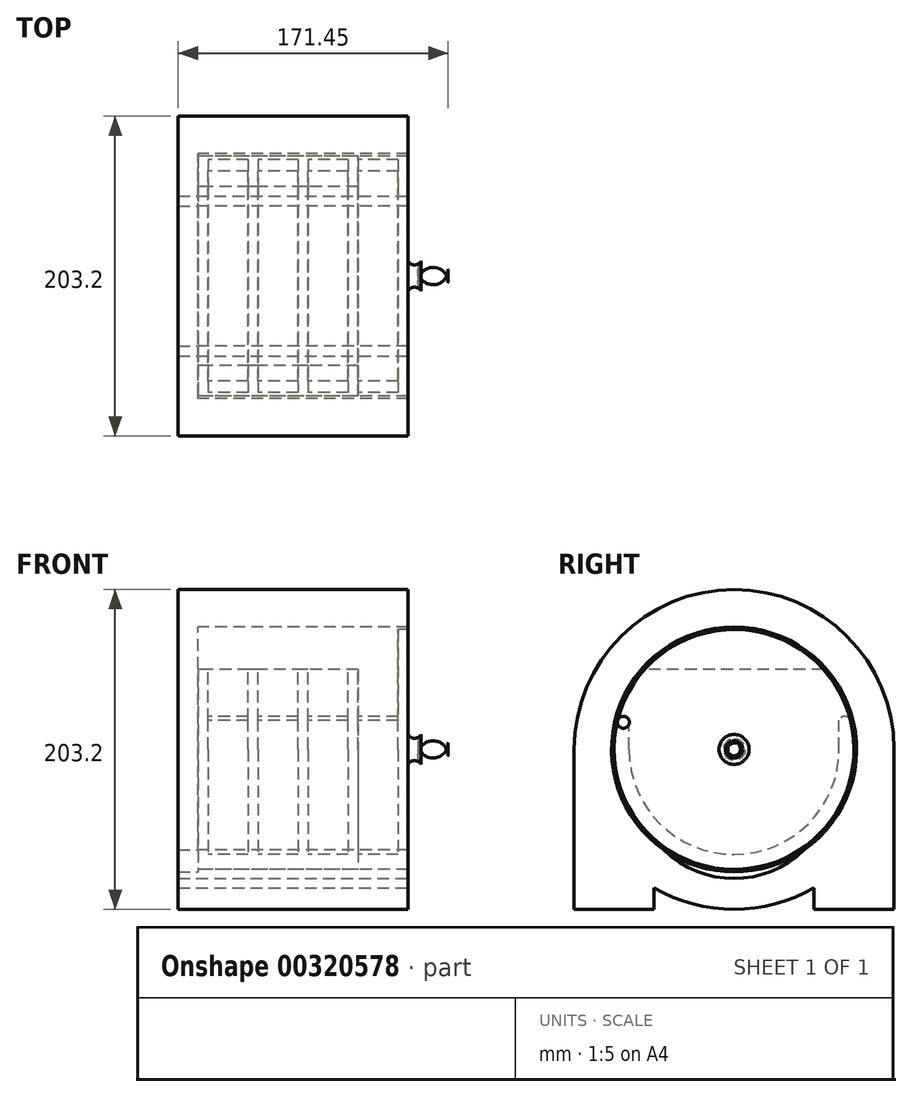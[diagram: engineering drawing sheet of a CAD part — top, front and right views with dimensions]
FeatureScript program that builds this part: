
annotation { "Feature Type Name" : "Feature", "Feature Type Description" : "" }
export const myFeature = defineFeature(function(context is Context, id is Id, definition is map)
    precondition{}
    {
        {
            var Q0;
            Q0=qCreatedBy(makeId("Right.planeOp"),FACE);
            var sketch = newSketch(context, id + "F0", { "sketchPlane" : qUnion([Q0])});
            skCircle(sketch, "E0", {"center": v(0, 0) * mm, "radius": 76.2 * mm});
            skLineSegment(sketch, "E1", {"start": v(0, 76.2) * mm, "end": v(0, 50.8) * mm});
            skLineSegment(sketch, "E2", {"start": v(56.8, 50.8) * mm, "end": v(-56.8, 50.8) * mm});
            skSolve(sketch);
        }
        {
            var Q0;
            {var subQ0=sQuery(id+"F0.wireOp",EDGE,"E2");var subQ1=sQuery(id+"F0.wireOp",EDGE,"E0");var subQ2=makeQuery(id+"F0.imprint","INTERSECT",VERTEX,{"disambiguationData":[OD(0.0)],"derivedFrom":[subQ1,subQ0]});Q0=makeQuery(id+"F0.imprint","IMPRINT",FACE,{"disambiguationData":[TD([[makeQuery(id+"F0.imprint","IMPRINT",EDGE,{"disambiguationData":[TD([[subQ2,1.0]])],"derivedFrom":subQ1}),1.0]])]});}
            extrude(context, id + "F1", {"entities" : qUnion([Q0]), "depth" : 6.35 * mm});
        }
        {
            var Q0;
            Q0=makeQuery(id+"F1.opExtrude","CAP_FACE",FACE,{"disambiguationData":[OSD([sQuery(id+"F0.wireOp",EDGE,"E0"),sQuery(id+"F0.wireOp",EDGE,"E2")])],"isStart":false});
            var sketch = newSketch(context, id + "F2", { "sketchPlane" : qUnion([Q0])});
            skCircle(sketch, "E3", {"center": v(0, 0) * mm, "radius": 76.2 * mm});
            skCircle(sketch, "E4.0", {"center": v(0, 0) * mm, "radius": 66.67 * mm});
            skLineSegment(sketch, "E5", {"start": v(-66.67, 0) * mm, "end": v(-66.67, 36.9) * mm});
            skLineSegment(sketch, "E6", {"start": v(66.67, 0) * mm, "end": v(66.67, 36.9) * mm});
            skArc(sketch, "E7", {"start": v(73.93, 18.45) * mm, "mid": v(70.3, 21.1) * mm, "end": v(66.67, 18.45) * mm});
            skPoint(sketch, "E7.startSnap0", {"position": v(66.67, 18.45) * mm});
            skArc(sketch, "E8", {"start": v(-66.67, 18.45) * mm, "mid": v(-70.3, 21.1) * mm, "end": v(-73.93, 18.45) * mm});
            skPoint(sketch, "E8.endSnap0", {"position": v(-66.67, 18.45) * mm});
            skSolve(sketch);
        }
        {
            var Q0;
            {var subQ3=sQuery(id+"F2.wireOp",EDGE,"E7");Q0=makeQuery(id+"F2.imprint","IMPRINT",FACE,{"disambiguationData":[TD([[makeQuery(id+"F2.imprint","IMPRINT",EDGE,{"derivedFrom":subQ3}),1.0]])]});}
            extrude(context, id + "F3", {"entities" : qUnion([Q0]), "operationType" : NewBodyOperationType.ADD, "depth" : 25.4 * mm});
        }
        {
            var Q0;
            Q0=makeQuery(id+"F3.opExtrude","CAP_FACE",FACE,{"disambiguationData":[OSD([sQuery(id+"F2.wireOp",EDGE,"E3"),sQuery(id+"F2.wireOp",EDGE,"E4.0"),sQuery(id+"F2.wireOp",EDGE,"E5"),sQuery(id+"F2.wireOp",EDGE,"E6"),sQuery(id+"F2.wireOp",EDGE,"E7"),sQuery(id+"F2.wireOp",EDGE,"E8")])],"isStart":false});
            var sketch = newSketch(context, id + "F4", { "sketchPlane" : qUnion([Q0])});
            skCircle(sketch, "E9", {"center": v(0, 0) * mm, "radius": 76.2 * mm});
            skLineSegment(sketch, "E10", {"start": v(0, 76.2) * mm, "end": v(0, 50.8) * mm});
            skLineSegment(sketch, "E11", {"start": v(56.8, 50.8) * mm, "end": v(-56.8, 50.8) * mm});
            skSolve(sketch);
        }
        {
            var Q0;
            Q0=makeQuery(id+"F4.imprint","IMPRINT",FACE,{"disambiguationData":[TD([[makeQuery(id+"F4.imprint","IMPRINT",EDGE,{"derivedFrom":makeQuery(id+"F3.opExtrude","CAP_EDGE",EDGE,{"disambiguationData":[OSD([sQuery(id+"F2.wireOp",EDGE,"E4.0")])],"isStart":false})}),-1.0]])]});
            var Q1;
            Q1=makeQuery(id+"F4.imprint","IMPRINT",FACE,{"disambiguationData":[TD([[makeQuery(id+"F4.imprint","IMPRINT",EDGE,{"derivedFrom":makeQuery(id+"F3.opExtrude","CAP_EDGE",EDGE,{"disambiguationData":[OSD([sQuery(id+"F2.wireOp",EDGE,"E4.0")])],"isStart":false})}),1.0]])]});
            extrude(context, id + "F5", {"entities" : qUnion([Q0, Q1]), "operationType" : NewBodyOperationType.ADD, "depth" : 6.35 * mm});
        }
        {
            var Q0;
            Q0=makeQuery(id+"F5.opExtrude","CAP_FACE",FACE,{"disambiguationData":[OSD([sQuery(id+"F4.wireOp",EDGE,"E9"),sQuery(id+"F4.wireOp",EDGE,"E11")])],"isStart":false});
            var sketch = newSketch(context, id + "F6", { "sketchPlane" : qUnion([Q0])});
            skCircle(sketch, "E12", {"center": v(0, 0) * mm, "radius": 76.2 * mm});
            skCircle(sketch, "E13.0", {"center": v(0, 0) * mm, "radius": 66.67 * mm});
            skLineSegment(sketch, "E14", {"start": v(-66.67, 0) * mm, "end": v(-66.67, 36.9) * mm});
            skLineSegment(sketch, "E15", {"start": v(66.67, 0) * mm, "end": v(66.67, 36.9) * mm});
            skArc(sketch, "E16", {"start": v(73.93, 18.45) * mm, "mid": v(70.3, 21.1) * mm, "end": v(66.67, 18.45) * mm});
            skPoint(sketch, "E16.startSnap0", {"position": v(66.67, 18.45) * mm});
            skArc(sketch, "E17", {"start": v(-66.67, 18.45) * mm, "mid": v(-70.3, 21.1) * mm, "end": v(-73.93, 18.45) * mm});
            skPoint(sketch, "E17.endSnap0", {"position": v(-66.67, 18.45) * mm});
            skSolve(sketch);
        }
        {
            var Q0;
            {var subQ3=sQuery(id+"F6.wireOp",EDGE,"E16");Q0=makeQuery(id+"F6.imprint","IMPRINT",FACE,{"disambiguationData":[TD([[makeQuery(id+"F6.imprint","IMPRINT",EDGE,{"derivedFrom":subQ3}),1.0]])]});}
            extrude(context, id + "F7", {"entities" : qUnion([Q0]), "operationType" : NewBodyOperationType.ADD, "depth" : 25.4 * mm});
        }
        {
            var Q0;
            Q0=makeQuery(id+"F7.opExtrude","CAP_FACE",FACE,{"disambiguationData":[OSD([sQuery(id+"F6.wireOp",EDGE,"E12"),sQuery(id+"F6.wireOp",EDGE,"E13.0"),sQuery(id+"F6.wireOp",EDGE,"E14"),sQuery(id+"F6.wireOp",EDGE,"E15"),sQuery(id+"F6.wireOp",EDGE,"E16"),sQuery(id+"F6.wireOp",EDGE,"E17")])],"isStart":false});
            var sketch = newSketch(context, id + "F8", { "sketchPlane" : qUnion([Q0])});
            skCircle(sketch, "E18", {"center": v(0, 0) * mm, "radius": 76.2 * mm});
            skLineSegment(sketch, "E19", {"start": v(0, 76.2) * mm, "end": v(0, 50.8) * mm});
            skLineSegment(sketch, "E20", {"start": v(56.8, 50.8) * mm, "end": v(-56.8, 50.8) * mm});
            skSolve(sketch);
        }
        {
            var Q0;
            Q0=makeQuery(id+"F8.imprint","IMPRINT",FACE,{"disambiguationData":[TD([[makeQuery(id+"F8.imprint","IMPRINT",EDGE,{"derivedFrom":makeQuery(id+"F7.opExtrude","CAP_EDGE",EDGE,{"disambiguationData":[OSD([sQuery(id+"F6.wireOp",EDGE,"E13.0")])],"isStart":false})}),-1.0]])]});
            var Q1;
            Q1=makeQuery(id+"F8.imprint","IMPRINT",FACE,{"disambiguationData":[TD([[makeQuery(id+"F8.imprint","IMPRINT",EDGE,{"derivedFrom":makeQuery(id+"F7.opExtrude","CAP_EDGE",EDGE,{"disambiguationData":[OSD([sQuery(id+"F6.wireOp",EDGE,"E13.0")])],"isStart":false})}),1.0]])]});
            extrude(context, id + "F9", {"entities" : qUnion([Q0, Q1]), "operationType" : NewBodyOperationType.ADD, "depth" : 6.35 * mm});
        }
        {
            var Q0;
            Q0=makeQuery(id+"F9.opExtrude","CAP_FACE",FACE,{"disambiguationData":[OSD([sQuery(id+"F8.wireOp",EDGE,"E18"),sQuery(id+"F8.wireOp",EDGE,"E20")])],"isStart":false});
            var sketch = newSketch(context, id + "F10", { "sketchPlane" : qUnion([Q0])});
            skCircle(sketch, "E21", {"center": v(0, 0) * mm, "radius": 76.2 * mm});
            skCircle(sketch, "E22.0", {"center": v(0, 0) * mm, "radius": 66.67 * mm});
            skLineSegment(sketch, "E23", {"start": v(-66.68, 0) * mm, "end": v(-66.68, 36.9) * mm});
            skLineSegment(sketch, "E24", {"start": v(66.67, 0) * mm, "end": v(66.67, 36.9) * mm});
            skArc(sketch, "E25", {"start": v(73.93, 18.45) * mm, "mid": v(70.3, 21.1) * mm, "end": v(66.68, 18.45) * mm});
            skPoint(sketch, "E25.startSnap0", {"position": v(66.67, 18.45) * mm});
            skArc(sketch, "E26", {"start": v(-66.68, 18.45) * mm, "mid": v(-70.3, 21.1) * mm, "end": v(-73.93, 18.45) * mm});
            skPoint(sketch, "E26.endSnap0", {"position": v(-66.68, 18.45) * mm});
            skSolve(sketch);
        }
        {
            var Q0;
            {var subQ3=sQuery(id+"F10.wireOp",EDGE,"E25");Q0=makeQuery(id+"F10.imprint","IMPRINT",FACE,{"disambiguationData":[TD([[makeQuery(id+"F10.imprint","IMPRINT",EDGE,{"derivedFrom":subQ3}),1.0]])]});}
            extrude(context, id + "F11", {"entities" : qUnion([Q0]), "operationType" : NewBodyOperationType.ADD, "depth" : 25.4 * mm});
        }
        {
            var Q0;
            Q0=makeQuery(id+"F11.opExtrude","CAP_FACE",FACE,{"disambiguationData":[OSD([sQuery(id+"F10.wireOp",EDGE,"E21"),sQuery(id+"F10.wireOp",EDGE,"E22.0"),sQuery(id+"F10.wireOp",EDGE,"E23"),sQuery(id+"F10.wireOp",EDGE,"E24"),sQuery(id+"F10.wireOp",EDGE,"E25"),sQuery(id+"F10.wireOp",EDGE,"E26")])],"isStart":false});
            var sketch = newSketch(context, id + "F12", { "sketchPlane" : qUnion([Q0])});
            skCircle(sketch, "E27", {"center": v(0, 0) * mm, "radius": 76.2 * mm});
            skLineSegment(sketch, "E28", {"start": v(0, 76.2) * mm, "end": v(0, 50.8) * mm});
            skLineSegment(sketch, "E29", {"start": v(56.8, 50.8) * mm, "end": v(-56.8, 50.8) * mm});
            skSolve(sketch);
        }
        {
            var Q0;
            Q0=makeQuery(id+"F12.imprint","IMPRINT",FACE,{"disambiguationData":[TD([[makeQuery(id+"F12.imprint","IMPRINT",EDGE,{"derivedFrom":makeQuery(id+"F11.opExtrude","CAP_EDGE",EDGE,{"disambiguationData":[OSD([sQuery(id+"F10.wireOp",EDGE,"E22.0")])],"isStart":false})}),-1.0]])]});
            var Q1;
            Q1=makeQuery(id+"F12.imprint","IMPRINT",FACE,{"disambiguationData":[TD([[makeQuery(id+"F12.imprint","IMPRINT",EDGE,{"derivedFrom":makeQuery(id+"F11.opExtrude","CAP_EDGE",EDGE,{"disambiguationData":[OSD([sQuery(id+"F10.wireOp",EDGE,"E22.0")])],"isStart":false})}),1.0]])]});
            extrude(context, id + "F13", {"entities" : qUnion([Q0, Q1]), "operationType" : NewBodyOperationType.ADD, "depth" : 6.35 * mm});
        }
        {
            var Q0;
            Q0=makeQuery(id+"F13.opExtrude","CAP_FACE",FACE,{"disambiguationData":[OSD([sQuery(id+"F12.wireOp",EDGE,"E27"),sQuery(id+"F12.wireOp",EDGE,"E29")])],"isStart":false});
            var sketch = newSketch(context, id + "F14", { "sketchPlane" : qUnion([Q0])});
            skCircle(sketch, "E30", {"center": v(0, 0) * mm, "radius": 76.2 * mm});
            skCircle(sketch, "E31.0", {"center": v(0, 0) * mm, "radius": 66.67 * mm});
            skLineSegment(sketch, "E32", {"start": v(-66.67, 0) * mm, "end": v(-66.67, 36.9) * mm});
            skLineSegment(sketch, "E33", {"start": v(66.67, 0) * mm, "end": v(66.67, 36.9) * mm});
            skArc(sketch, "E34", {"start": v(73.93, 18.45) * mm, "mid": v(70.3, 21.1) * mm, "end": v(66.68, 18.45) * mm});
            skPoint(sketch, "E34.startSnap0", {"position": v(66.67, 18.45) * mm});
            skArc(sketch, "E35", {"start": v(-66.67, 18.45) * mm, "mid": v(-70.3, 21.1) * mm, "end": v(-73.93, 18.45) * mm});
            skPoint(sketch, "E35.endSnap0", {"position": v(-66.68, 18.45) * mm});
            skSolve(sketch);
        }
        {
            var Q0;
            {var subQ3=sQuery(id+"F14.wireOp",EDGE,"E34");Q0=makeQuery(id+"F14.imprint","IMPRINT",FACE,{"disambiguationData":[TD([[makeQuery(id+"F14.imprint","IMPRINT",EDGE,{"derivedFrom":subQ3}),1.0]])]});}
            extrude(context, id + "F15", {"entities" : qUnion([Q0]), "operationType" : NewBodyOperationType.ADD, "depth" : 25.4 * mm});
        }
        {
            var Q0;
            Q0=makeQuery(id+"F15.opExtrude","CAP_FACE",FACE,{"disambiguationData":[OSD([sQuery(id+"F14.wireOp",EDGE,"E30"),sQuery(id+"F14.wireOp",EDGE,"E31.0"),sQuery(id+"F14.wireOp",EDGE,"E32"),sQuery(id+"F14.wireOp",EDGE,"E33"),sQuery(id+"F14.wireOp",EDGE,"E34"),sQuery(id+"F14.wireOp",EDGE,"E35")])],"isStart":false});
            var sketch = newSketch(context, id + "F16", { "sketchPlane" : qUnion([Q0])});
            skCircle(sketch, "E36", {"center": v(0, 0) * mm, "radius": 76.2 * mm});
            skLineSegment(sketch, "E37", {"start": v(0, 76.2) * mm, "end": v(0, 50.8) * mm});
            skLineSegment(sketch, "E38", {"start": v(56.8, 50.8) * mm, "end": v(-56.8, 50.8) * mm});
            skSolve(sketch);
        }
        {
            var Q0;
            Q0=makeQuery(id+"F16.imprint","IMPRINT",FACE,{"disambiguationData":[TD([[makeQuery(id+"F16.imprint","IMPRINT",EDGE,{"derivedFrom":makeQuery(id+"F15.opExtrude","CAP_EDGE",EDGE,{"disambiguationData":[OSD([sQuery(id+"F14.wireOp",EDGE,"E31.0")])],"isStart":false})}),-1.0]])]});
            var Q1;
            Q1=makeQuery(id+"F16.imprint","IMPRINT",FACE,{"disambiguationData":[TD([[makeQuery(id+"F16.imprint","IMPRINT",EDGE,{"derivedFrom":makeQuery(id+"F15.opExtrude","CAP_EDGE",EDGE,{"disambiguationData":[OSD([sQuery(id+"F14.wireOp",EDGE,"E31.0")])],"isStart":false})}),1.0]])]});
            var Q2;
            {var subQ0=sQuery(id+"F16.wireOp",EDGE,"E37");Q2=makeQuery(id+"F16.imprint","IMPRINT",FACE,{"disambiguationData":[TD([[makeQuery(id+"F16.imprint","IMPRINT",EDGE,{"derivedFrom":subQ0}),-1.0]])]});}
            var Q3;
            {var subQ0=sQuery(id+"F16.wireOp",EDGE,"E37");Q3=makeQuery(id+"F16.imprint","IMPRINT",FACE,{"disambiguationData":[TD([[makeQuery(id+"F16.imprint","IMPRINT",EDGE,{"derivedFrom":subQ0}),1.0]])]});}
            extrude(context, id + "F17", {"entities" : qUnion([Q0, Q1, Q2, Q3]), "operationType" : NewBodyOperationType.ADD, "depth" : 6.35 * mm});
        }
        {
            var Q0;
            Q0=makeQuery(id+"F1.opExtrude","CAP_FACE",FACE,{"disambiguationData":[OSD([sQuery(id+"F0.wireOp",EDGE,"E0"),sQuery(id+"F0.wireOp",EDGE,"E2")])],"isStart":true});
            var sketch = newSketch(context, id + "F18", { "sketchPlane" : qUnion([Q0])});
            skArc(sketch, "E39", {"start": v(101.6, 0) * mm, "mid": v(0, 101.6) * mm, "end": v(-101.6, 0) * mm});
            skCircle(sketch, "E40", {"center": v(0, 0) * mm, "radius": 77.79 * mm});
            skLineSegment(sketch, "E41", {"start": v(-101.6, 0) * mm, "end": v(-101.6, -108.32) * mm});
            skLineSegment(sketch, "E42", {"start": v(-50.8, -101.6) * mm, "end": v(-101.6, -101.6) * mm});
            skLineSegment(sketch, "E43", {"start": v(101.6, 0) * mm, "end": v(101.6, -111.12) * mm});
            skLineSegment(sketch, "E44", {"start": v(50.8, -101.6) * mm, "end": v(101.6, -101.6) * mm});
            skLineSegment(sketch, "E45", {"start": v(-50.8, -101.6) * mm, "end": v(-50.8, -87.99) * mm});
            skLineSegment(sketch, "E46", {"start": v(50.8, -101.6) * mm, "end": v(50.8, -87.99) * mm});
            skLineSegment(sketch, "E47", {"start": v(50.8, -87.99) * mm, "end": v(50.8, -87.99) * mm});
            skLineSegment(sketch, "E48", {"start": v(60.26, -51.22) * mm, "end": v(64.62, -43.3) * mm});
            skPoint(sketch, "E49.visualSharp", {"position": v(50.8, -68.39) * mm});
            skArc(sketch, "E49.filletArc", {"start": v(60.26, -51.22) * mm, "mid": v(53.2, -69) * mm, "end": v(50.8, -87.99) * mm});
            skArc(sketch, "E50", {"start": v(-44.45, -63.84) * mm, "mid": v(0, -81.99) * mm, "end": v(44.45, -63.84) * mm});
            skArc(sketch, "E51.trimOffspring", {"start": v(-50.8, -87.99) * mm, "mid": v(0, -101.6) * mm, "end": v(50.8, -87.99) * mm});
            skPoint(sketch, "E52.orphan", {"position": v(0, -101.6) * mm});
            skSolve(sketch);
        }
        {
            var Q0;
            Q0=makeQuery(id+"F18.imprint","IMPRINT",FACE,{"disambiguationData":[TD([[makeQuery(id+"F18.imprint","IMPRINT",EDGE,{"derivedFrom":sQuery(id+"F18.wireOp",EDGE,"E40")}),-1.0]])]});
            var Q1;
            Q1=makeQuery(id+"F18.imprint","IMPRINT",FACE,{"disambiguationData":[TD([[makeQuery(id+"F18.imprint","IMPRINT",EDGE,{"derivedFrom":sQuery(id+"F18.wireOp",EDGE,"E40")}),1.0]])]});
            var Q2;
            Q2=makeQuery(id+"F18.imprint","IMPRINT",FACE,{"disambiguationData":[TD([[makeQuery(id+"F18.imprint","IMPRINT",EDGE,{"derivedFrom":makeQuery(id+"F1.opExtrude","CAP_EDGE",EDGE,{"disambiguationData":[OSD([sQuery(id+"F0.wireOp",EDGE,"E0")])],"isStart":true})}),-1.0]])]});
            var Q3;
            {var subQ3=sQuery(id+"F18.wireOp",EDGE,"E45");Q3=makeQuery(id+"F18.imprint","IMPRINT",FACE,{"disambiguationData":[TD([[makeQuery(id+"F18.imprint","IMPRINT",EDGE,{"derivedFrom":subQ3}),1.0]])]});}
            var Q4;
            {var subQ3=sQuery(id+"F18.wireOp",EDGE,"E46");Q4=makeQuery(id+"F18.imprint","IMPRINT",FACE,{"disambiguationData":[TD([[makeQuery(id+"F18.imprint","IMPRINT",EDGE,{"derivedFrom":subQ3}),-1.0]])]});}
            extrude(context, id + "F19", {"entities" : qUnion([Q0, Q1, Q2, Q3, Q4]), "depth" : 12.7 * mm});
        }
        {
            var Q0;
            Q0=makeQuery(id+"F18.imprint","IMPRINT",FACE,{"disambiguationData":[TD([[makeQuery(id+"F18.imprint","IMPRINT",EDGE,{"derivedFrom":sQuery(id+"F18.wireOp",EDGE,"E40")}),-1.0]])]});
            var Q1;
            {var subQ3=sQuery(id+"F18.wireOp",EDGE,"E46");Q1=makeQuery(id+"F18.imprint","IMPRINT",FACE,{"disambiguationData":[TD([[makeQuery(id+"F18.imprint","IMPRINT",EDGE,{"derivedFrom":subQ3}),-1.0]])]});}
            var Q2;
            {var subQ3=sQuery(id+"F18.wireOp",EDGE,"E45");Q2=makeQuery(id+"F18.imprint","IMPRINT",FACE,{"disambiguationData":[TD([[makeQuery(id+"F18.imprint","IMPRINT",EDGE,{"derivedFrom":subQ3}),1.0]])]});}
            var Q3;
            Q3=makeQuery(id+"F17.opExtrude","CAP_FACE",FACE,{"disambiguationData":[OSD([sQuery(id+"F16.wireOp",EDGE,"E36")])],"isStart":false});
            extrude(context, id + "F20", {"entities" : qUnion([Q0, Q1, Q2]), "operationType" : NewBodyOperationType.ADD, "endBound" : BoundingType.UP_TO_SURFACE, "oppositeDirection" : true, "endBoundEntityFace" : qUnion([Q3]), "depth" : 25.4 * mm});
        }
        {
            var Q0;
            Q0=makeQuery(id+"F17.opExtrude","CAP_FACE",FACE,{"disambiguationData":[OSD([sQuery(id+"F16.wireOp",EDGE,"E36")])],"isStart":false});
            var sketch = newSketch(context, id + "F21", { "sketchPlane" : qUnion([Q0])});
            skLineSegment(sketch, "E53", {"start": v(0, 0) * mm, "end": v(0, 4.03) * mm});
            skLineSegment(sketch, "E54", {"start": v(0, 4.03) * mm, "end": v(3.6, 4.03) * mm});
            skLineSegment(sketch, "E55", {"start": v(3.6, 4.03) * mm, "end": v(3.6, 0) * mm});
            skLineSegment(sketch, "E56", {"start": v(3.6, 0) * mm, "end": v(0, 0) * mm});
            skSolve(sketch);
        }
        {
            var Q0;
            Q0=makeQuery(id+"F21.imprint","IMPRINT",FACE,{"disambiguationData":[TD([[makeQuery(id+"F21.imprint","IMPRINT",EDGE,{"derivedFrom":sQuery(id+"F21.wireOp",EDGE,"E53")}),-1.0]])]});
            extrude(context, id + "F22", {"entities" : qUnion([Q0]), "operationType" : NewBodyOperationType.ADD, "depth" : 25.4 * mm});
        }
        {
            var Q0;
            Q0=makeQuery(id+"F22.opExtrude","SWEPT_FACE",FACE,{"disambiguationData":[OSD([sQuery(id+"F21.wireOp",EDGE,"E53")])]});
            var sketch = newSketch(context, id + "F23", { "sketchPlane" : qUnion([Q0])});
            skLineSegment(sketch, "E57", {"start": v(133.35, 0) * mm, "end": v(133.35, 9.53) * mm});
            skArc(sketch, "E58", {"start": v(158.75, 4.03) * mm, "mid": v(149.22, 13.56) * mm, "end": v(139.7, 4.03) * mm});
            skArc(sketch, "E59", {"start": v(133.35, 9.53) * mm, "mid": v(137.4, 7.08) * mm, "end": v(141.44, 9.53) * mm});
            skLineSegment(sketch, "E60", {"start": v(158.75, 4.03) * mm, "end": v(158.75, 0) * mm});
            skLineSegment(sketch, "E61", {"start": v(133.35, 0) * mm, "end": v(158.75, 0) * mm});
            skSolve(sketch);
        }
        {
            var Q0;
            {var subQ0=sQuery(id+"F23.wireOp",EDGE,"E58");var subQ3=sQuery(id+"F23.wireOp",EDGE,"E59");var subQ4=makeQuery(id+"F23.imprint","INTERSECT",VERTEX,{"disambiguationData":[OD(0.0)],"derivedFrom":[subQ0,subQ3]});Q0=makeQuery(id+"F23.imprint","IMPRINT",FACE,{"disambiguationData":[TD([[makeQuery(id+"F23.imprint","IMPRINT",EDGE,{"disambiguationData":[TD([[subQ4,1.0]])],"derivedFrom":subQ3}),-1.0]])]});}
            var Q1;
            {var subQ0=sQuery(id+"F23.wireOp",EDGE,"E57");var subQ3=sQuery(id+"F23.wireOp",EDGE,"E59");var subQ4=makeQuery(id+"F23.imprint","INTERSECT",VERTEX,{"derivedFrom":[subQ0,subQ3]});Q1=makeQuery(id+"F23.imprint","IMPRINT",FACE,{"disambiguationData":[TD([[makeQuery(id+"F23.imprint","IMPRINT",EDGE,{"disambiguationData":[TD([[subQ4,-1.0]])],"derivedFrom":subQ3}),-1.0]])]});}
            var Q2;
            {var subQ0=sQuery(id+"F23.wireOp",EDGE,"E60");Q2=makeQuery(id+"F23.imprint","IMPRINT",FACE,{"disambiguationData":[TD([[makeQuery(id+"F23.imprint","IMPRINT",EDGE,{"derivedFrom":subQ0}),1.0]])]});}
            var Q3;
            Q3=sQuery(id+"F23.wireOp",EDGE,"E61");
            revolve(context, id + "F24", {"operationType" : NewBodyOperationType.ADD, "entities" : qUnion([Q0, Q1, Q2]), "axis" : qUnion([Q3]), "revolveType" : RevolveType.FULL});
        }
        {
            var Q0;
            {var subQ0=sQuery(id+"F0.wireOp",EDGE,"E2");var subQ1=sQuery(id+"F0.wireOp",EDGE,"E0");var subQ2=makeQuery(id+"F0.imprint","INTERSECT",VERTEX,{"disambiguationData":[OD(0.0)],"derivedFrom":[subQ1,subQ0]});Q0=makeQuery(id+"F0.imprint","IMPRINT",FACE,{"disambiguationData":[TD([[makeQuery(id+"F0.imprint","IMPRINT",EDGE,{"disambiguationData":[TD([[subQ2,1.0]])],"derivedFrom":subQ1}),1.0]])]});}
            extrude(context, id + "F25", {"entities" : qUnion([Q0]), "depth" : 101.6 * mm});
        }
    });
